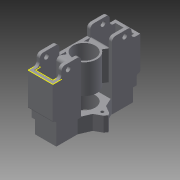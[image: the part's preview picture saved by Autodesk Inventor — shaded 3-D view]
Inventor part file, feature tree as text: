
AUTODESK INVENTOR PART (.ipt)
format: ipt  version: 2013 SP2 (Build 170200200, 200)  size: 534,016 bytes
history: native  units: in
note: dims shown in document units (in); Inventor stores cm internally (conversion verified against a paired STEP export)
features: sketch x19, extrude x18, thicken_offset x13, fillet x7, mirror x1
ambient origin geometry x8: Origin, YZ Plane, XZ Plane, XY Plane, X Axis, Y Axis, Z Axis, Center Point
bodies: Solid1 (feature_tree)
feature tree (58):
  extrude  "Extrusion1"  Depth=0.125in
  extrude  "Extrusion2"  Depth=0.125in
  fillet  "Fillet2"  Radius=0.125in
  fillet  "Fillet3"  Radius=1.137in
  sketch  "Sketch4"  dims[d15=0.595in d16=0.595in]
  extrude  "Extrusion4"  Depth=0.595in
  extrude  "Extrusion5"  Depth=0.325in TaperAngle=0.0deg
  extrude  "Extrusion6"  Depth=0.05in
  extrude  "Extrusion7"  Depth=0.061in
  extrude  "Extrusion8"  Depth=0.125in
  extrude  "Extrusion9"  Depth=0.085in
  sketch  "Sketch11"  dims[d57=0.006in d59=0.006in]
  thicken_offset  "Thicken1"
  thicken_offset  "Thicken2"
  fillet  "Fillet10"  Radius=0.36in
  fillet  "Fillet12"  Radius=1.0in
  fillet  "Fillet13"  Radius=0.36in
  fillet  "Fillet14"  Radius=0.36in
  thicken_offset  "Thicken3"
  thicken_offset  "Thicken4"
  thicken_offset  "Thicken5"
  thicken_offset  "Thicken6"
  thicken_offset  "Thicken7"
  thicken_offset  "Thicken8"
  thicken_offset  "Thicken9"
  thicken_offset  "Thicken10"
  thicken_offset  "Thicken11"
  thicken_offset  "Thicken12"
  thicken_offset  "Thicken13"
  extrude  "Extrusion15"  Depth=0.006in
  mirror  "Mirror3"
  extrude  "Extrusion16"  Depth=0.325in TaperAngle=0.0deg
  extrude  "Extrusion17"  Depth=0.01in
  extrude  "Extrusion18"  Depth=0.01in
  extrude  "Extrusion19"  Depth=0.05in
  fillet  "Fillet17"  Radius=0.164in
  extrude  "Extrusion21"  Depth=0.05in
  sketch  "Sketch31"  dims[d79=0.01in d80=0.01in]
  extrude  "Extrusion22"  Depth=0.01in
  sketch  "Sketch33"  dims[d83=0.01in d84=0.01in]
  extrude  "Extrusion24"  Depth=0.01in
  extrude  "Extrusion25"  Depth=0.01in
  extrude  "Extrusion26"  Depth=0.01in
  sketch  "Sketch1"  dims[d8=0.717in d9=0.125in]
  sketch  "Sketch2"  dims[d10=0.125in d11=0.125in d12=0.125in d13=1.137in d14=0.0in]
  sketch  "Sketch5"  dims[d17=0.125in d18=0.325in d19=0.0in]
  sketch  "Sketch6"  dims[d21=0.05in d22=0.05in]
  sketch  "Sketch7"  dims[d23=0.0605in d25=0.061in]
  sketch  "Sketch8"  dims[d28=0.125in d30=0.125in]
  sketch  "Sketch10"  dims[d33=0.173in d35=0.085in d37=0.36in d38=0.0in d43=1.0in d44=0.0in d45=0.36in d46=0.0in d50=0.36in d51=0.0in]
  sketch  "Sketch18"  dims[d60=0.5in d61=0.0in d62=0.325in d63=0.0in]
  sketch  "Sketch19"  dims[d64=0.01in d65=0.01in]
  sketch  "Sketch20"  dims[d66=0.01in d67=0.01in]
  sketch  "Sketch21"  dims[d68=0.125in d70=0.05in d72=0.164in]
  sketch  "Sketch22"  dims[d73=0.05in d74=0.05in]
  sketch  "Sketch30"  dims[d77=0.01in d78=0.01in]
  sketch  "Sketch32"  dims[d81=0.01in d82=0.01in]
  sketch  "Sketch34"  dims[d85=0.01in d86=0.01in d87=0.01in d88=0.01in d89=0.01in d90=0.01in d91=0.01in d92=0.01in d93=0.01in d94=0.01in d95=0.02in d96=0.02in d97=0.02in d98=0.02in d111=0.935in d119=0.15in d122=0.75in d123=1.0in d124=0.0in d125=0.001in d126=0.0in d131=0.75in d132=0.875in d134=1.0in d135=0.0in d137=0.5in d138=0.0in d139=0.125in d140=0.0in d143=0.125in d148=1.5in d149=0.0in d152=1.1in d153=0.0in d160=0.2in d161=90.0deg d162=0.16in d163=0.5in d164=0.25in d165=0.0in d166=50.0in d167=0.0in d168=0.038in d169=1.0in d170=90.0deg d173=0.25in d174=0.16in d175=0.5in d176=0.0in]
